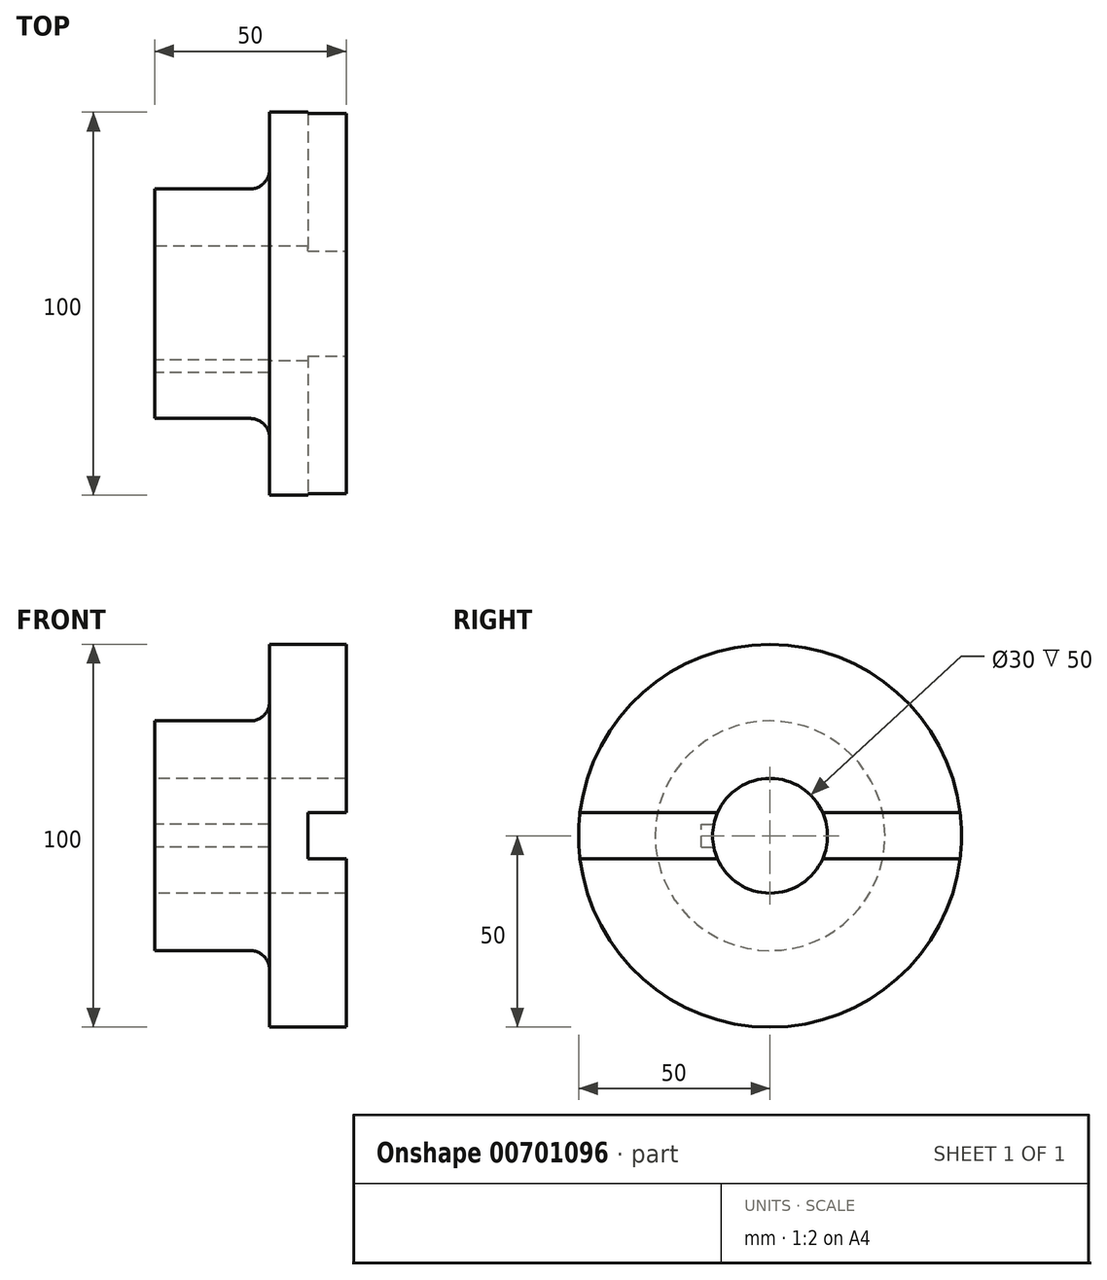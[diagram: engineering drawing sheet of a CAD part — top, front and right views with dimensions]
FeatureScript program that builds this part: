
annotation { "Feature Type Name" : "Feature", "Feature Type Description" : "" }
export const myFeature = defineFeature(function(context is Context, id is Id, definition is map)
    precondition{}
    {
        {
            var Q0;
            Q0=qCreatedBy(makeId("Top.planeOp"),FACE);
            var sketch = newSketch(context, id + "F0", { "sketchPlane" : qUnion([Q0])});
            skLineSegment(sketch, "E0", {"start": v(0, 0) * mm, "end": v(0, -30) * mm});
            skLineSegment(sketch, "E1", {"start": v(30, -30) * mm, "end": v(30, -50) * mm});
            skLineSegment(sketch, "E2", {"start": v(30, -50) * mm, "end": v(50, -50) * mm});
            skLineSegment(sketch, "E3", {"start": v(50, 0) * mm, "end": v(0, 0) * mm});
            skLineSegment(sketch, "E4", {"start": v(50, -50) * mm, "end": v(50, -6) * mm});
            skLineSegment(sketch, "E5", {"start": v(50, -6) * mm, "end": v(40, -6) * mm});
            skLineSegment(sketch, "E6", {"start": v(40, -6) * mm, "end": v(40, 0) * mm});
            skLineSegment(sketch, "E7", {"start": v(40, 0) * mm, "end": v(0, 0) * mm});
            skLineSegment(sketch, "E8", {"start": v(0, -30) * mm, "end": v(30, -30) * mm});
            skLineSegment(sketch, "E9", {"start": v(0, -15) * mm, "end": v(50, -15) * mm});
            skSolve(sketch);
        }
        {
            var Q0;
            {var subQ0=sQuery(id+"F0.wireOp",EDGE,"E5");Q0=makeQuery(id+"F0.imprint","IMPRINT",FACE,{"disambiguationData":[TD([[makeQuery(id+"F0.imprint","IMPRINT",EDGE,{"derivedFrom":subQ0}),1.0]])]});}
            var Q1;
            Q1=makeQuery(id+"F0.imprint","IMPRINT",FACE,{"disambiguationData":[TD([[makeQuery(id+"F0.imprint","IMPRINT",EDGE,{"derivedFrom":sQuery(id+"F0.wireOp",EDGE,"E1")}),1.0]])]});
            var Q2;
            Q2=sQuery(id+"F0.wireOp",EDGE,"E7");
            revolve(context, id + "F1", {"entities" : qUnion([Q0, Q1]), "axis" : qUnion([Q2]), "revolveType" : RevolveType.FULL});
        }
        {
            var Q0;
            Q0=makeQuery(id+"F1.opRevolve","SWEPT_FACE",FACE,{"disambiguationData":[OSD([sQuery(id+"F0.wireOp",EDGE,"E0")])]});
            var sketch = newSketch(context, id + "F2", { "sketchPlane" : qUnion([Q0])});
            skCircle(sketch, "E10", {"center": v(0, 0) * mm, "radius": 15 * mm});
            skSolve(sketch);
        }
        {
            var Q0;
            Q0 = qSketchRegion(id + "F2", true);
            extrude(context, id + "F3", {"entities" : qUnion([Q0]), "operationType" : NewBodyOperationType.REMOVE, "endBound" : BoundingType.THROUGH_ALL, "oppositeDirection" : true, "depth" : 25 * mm, "offsetDistance" : 25 * mm});
        }
        {
            var Q0;
            Q0=makeQuery(id+"F1.opRevolve","SWEPT_FACE",FACE,{"disambiguationData":[OSD([sQuery(id+"F0.wireOp",EDGE,"E0")])]});
            var sketch = newSketch(context, id + "F4", { "sketchPlane" : qUnion([Q0])});
            skLineSegment(sketch, "E11.bottom", {"start": v(18, -3) * mm, "end": v(12, -3) * mm});
            skLineSegment(sketch, "E11.top", {"start": v(18, 3) * mm, "end": v(12, 3) * mm});
            skLineSegment(sketch, "E11.left", {"start": v(18, -3) * mm, "end": v(18, 3) * mm});
            skLineSegment(sketch, "E11.right", {"start": v(12, -3) * mm, "end": v(12, 3) * mm});
            skPoint(sketch, "E11.middle", {"position": v(15, 0) * mm});
            skLineSegment(sketch, "E12", {"start": v(0, 0) * mm, "end": v(15, 0) * mm});
            skSolve(sketch);
        }
        {
            var Q0;
            {var subQ0=sQuery(id+"F4.wireOp",EDGE,"E11.left");Q0=makeQuery(id+"F4.imprint","IMPRINT",FACE,{"disambiguationData":[TD([[makeQuery(id+"F4.imprint","IMPRINT",EDGE,{"derivedFrom":subQ0}),1.0]])]});}
            var Q1;
            Q1=makeQuery(id+"F1.opRevolve","SWEPT_FACE",FACE,{"disambiguationData":[OSD([sQuery(id+"F0.wireOp",EDGE,"E1")])]});
            extrude(context, id + "F5", {"entities" : qUnion([Q0]), "operationType" : NewBodyOperationType.REMOVE, "endBound" : BoundingType.UP_TO_SURFACE, "oppositeDirection" : true, "depth" : 25 * mm, "endBoundEntityFace" : qUnion([Q1]), "offsetDistance" : 25 * mm});
        }
        {
            var Q0;
            Q0=makeQuery(id+"F1.opRevolve","SWEPT_FACE",FACE,{"disambiguationData":[OSD([sQuery(id+"F0.wireOp",EDGE,"E4")])]});
            var sketch = newSketch(context, id + "F6", { "sketchPlane" : qUnion([Q0])});
            skLineSegment(sketch, "E13.bottom", {"start": v(54.92, -6) * mm, "end": v(-54.92, -6) * mm});
            skLineSegment(sketch, "E13.top", {"start": v(54.92, 6) * mm, "end": v(-54.92, 6) * mm});
            skLineSegment(sketch, "E13.left", {"start": v(54.92, -6) * mm, "end": v(54.92, 6) * mm});
            skLineSegment(sketch, "E13.right", {"start": v(-54.92, -6) * mm, "end": v(-54.92, 6) * mm});
            skPoint(sketch, "E13.middle", {"position": v(0, 0) * mm});
            skSolve(sketch);
        }
        {
            var Q0;
            {var subQ0=sQuery(id+"F6.wireOp",EDGE,"E13.bottom");var subQ1=sQuery(id+"F0.wireOp",EDGE,"E4");var subQ2=makeQuery(id+"F1.opRevolve","SWEPT_EDGE",EDGE,{"disambiguationData":[OSD([sQuery(id+"F0.wireOp",EDGE,"E2"),subQ1])]});var subQ3=makeQuery(id+"F6.imprint","INTERSECT",VERTEX,{"disambiguationData":[OD(1.0)],"derivedFrom":[subQ2,subQ0]});Q0=makeQuery(id+"F6.imprint","IMPRINT",FACE,{"disambiguationData":[TD([[makeQuery(id+"F6.imprint","IMPRINT",EDGE,{"disambiguationData":[TD([[subQ3,1.0]])],"derivedFrom":subQ0}),-1.0]])]});}
            var Q1;
            {var subQ0=sQuery(id+"F6.wireOp",EDGE,"E13.bottom");var subQ1=sQuery(id+"F0.wireOp",EDGE,"E4");var subQ2=makeQuery(id+"F1.opRevolve","SWEPT_EDGE",EDGE,{"disambiguationData":[OSD([sQuery(id+"F0.wireOp",EDGE,"E2"),subQ1])]});var subQ3=makeQuery(id+"F6.imprint","INTERSECT",VERTEX,{"disambiguationData":[OD(0.0)],"derivedFrom":[subQ2,subQ0]});Q1=makeQuery(id+"F6.imprint","IMPRINT",FACE,{"disambiguationData":[TD([[makeQuery(id+"F6.imprint","IMPRINT",EDGE,{"disambiguationData":[TD([[subQ3,-1.0]])],"derivedFrom":subQ0}),-1.0]])]});}
            extrude(context, id + "F7", {"entities" : qUnion([Q0, Q1]), "operationType" : NewBodyOperationType.REMOVE, "oppositeDirection" : true, "depth" : 10 * mm, "offsetDistance" : 25 * mm});
        }
        {
            var Q0;
            Q0=makeQuery(id+"F1.opRevolve","SWEPT_EDGE",EDGE,{"disambiguationData":[OSD([sQuery(id+"F0.wireOp",EDGE,"E1"),sQuery(id+"F0.wireOp",EDGE,"E8")])]});
            fillet(context, id + "F8", {"entities" : qUnion([Q0]), "radius" : 5 * mm, "tangentPropagation" : true, "allowEdgeOverflow" : false});
        }
    });
